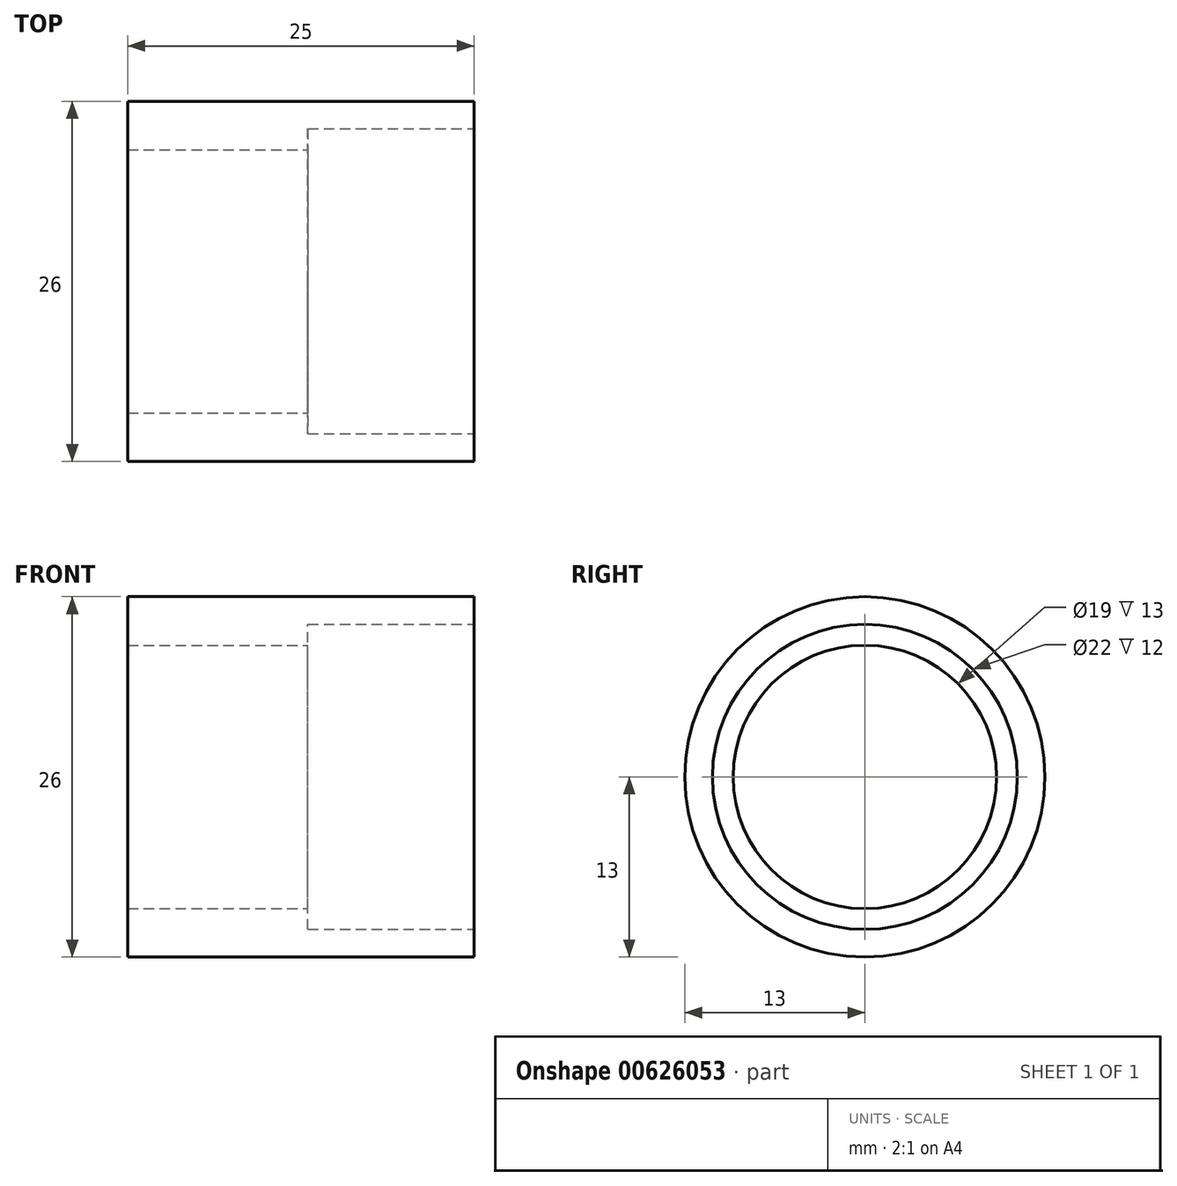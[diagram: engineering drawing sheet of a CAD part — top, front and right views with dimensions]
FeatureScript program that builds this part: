
annotation { "Feature Type Name" : "Feature", "Feature Type Description" : "" }
export const myFeature = defineFeature(function(context is Context, id is Id, definition is map)
    precondition{}
    {
        {
            var Q0;
            Q0=qCreatedBy(makeId("Front.planeOp"),FACE);
            var sketch = newSketch(context, id + "F0", { "sketchPlane" : qUnion([Q0])});
            skLineSegment(sketch, "E0", {"start": v(0, 0) * mm, "end": v(25, 0) * mm});
            skLineSegment(sketch, "E1", {"start": v(25, 0) * mm, "end": v(25, 13) * mm});
            skLineSegment(sketch, "E2", {"start": v(25, 13) * mm, "end": v(0, 13) * mm});
            skLineSegment(sketch, "E3", {"start": v(0, 13) * mm, "end": v(0, 0) * mm});
            skSolve(sketch);
        }
        {
            var Q0;
            Q0=makeQuery(id+"F0.imprint","IMPRINT",FACE,{"disambiguationData":[TD([[makeQuery(id+"F0.imprint","IMPRINT",EDGE,{"derivedFrom":sQuery(id+"F0.wireOp",EDGE,"E0")}),1.0]])]});
            var Q1;
            Q1=sQuery(id+"F0.wireOp",EDGE,"E0");
            revolve(context, id + "F1", {"entities" : qUnion([Q0]), "axis" : qUnion([Q1]), "revolveType" : RevolveType.FULL});
        }
        {
            var Q0;
            Q0=makeQuery(id+"F1.opRevolve","SWEPT_FACE",FACE,{"disambiguationData":[OSD([sQuery(id+"F0.wireOp",EDGE,"E1")])]});
            var sketch = newSketch(context, id + "F2", { "sketchPlane" : qUnion([Q0])});
            skCircle(sketch, "E4", {"center": v(0, 0) * mm, "radius": 9.5 * mm});
            skCircle(sketch, "E5", {"center": v(0, 0) * mm, "radius": 11 * mm});
            skSolve(sketch);
        }
        {
            var Q0;
            Q0=makeQuery(id+"F2.imprint","IMPRINT",FACE,{"disambiguationData":[TD([[makeQuery(id+"F2.imprint","IMPRINT",EDGE,{"derivedFrom":sQuery(id+"F2.wireOp",EDGE,"E4")}),1.0]])]});
            var Q1;
            Q1=sQuery(id+"F2.wireOp",EDGE,"E4");
            extrude(context, id + "F3", {"entities" : qUnion([Q0]), "operationType" : NewBodyOperationType.REMOVE, "surfaceEntities" : qUnion([Q1]), "oppositeDirection" : true, "depth" : 57.5 * mm, "offsetDistance" : 25 * mm});
        }
        {
            var Q0;
            Q0=makeQuery(id+"F2.imprint","IMPRINT",FACE,{"disambiguationData":[TD([[makeQuery(id+"F2.imprint","IMPRINT",EDGE,{"derivedFrom":sQuery(id+"F2.wireOp",EDGE,"E4")}),-1.0]])]});
            extrude(context, id + "F4", {"entities" : qUnion([Q0]), "operationType" : NewBodyOperationType.REMOVE, "oppositeDirection" : true, "depth" : 12 * mm, "offsetDistance" : 25 * mm});
        }
    });
